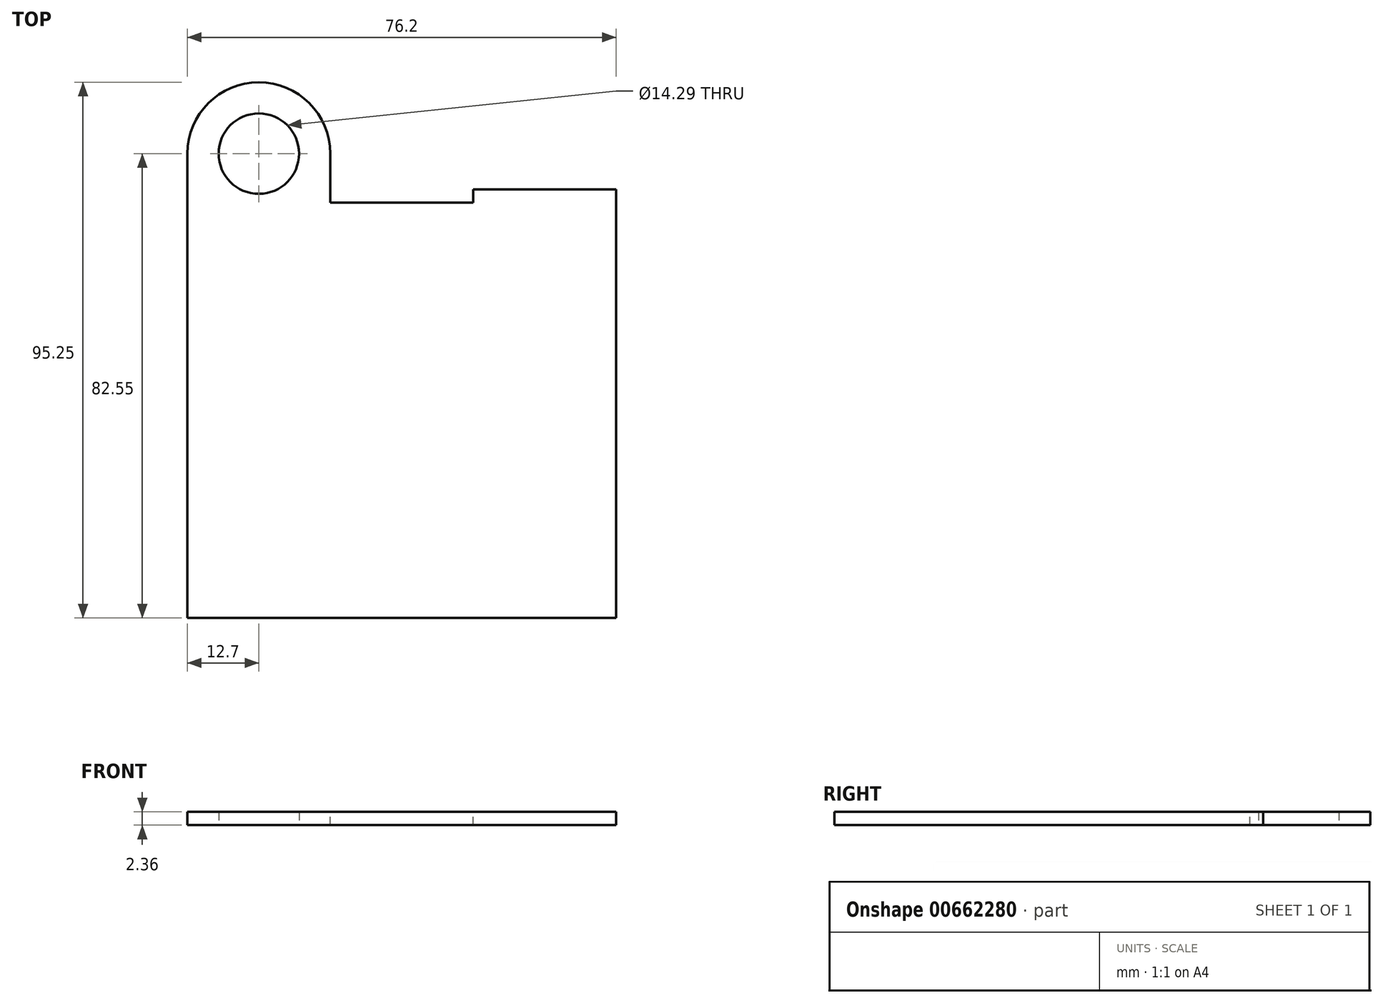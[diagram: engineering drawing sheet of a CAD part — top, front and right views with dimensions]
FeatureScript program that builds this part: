
annotation { "Feature Type Name" : "Feature", "Feature Type Description" : "" }
export const myFeature = defineFeature(function(context is Context, id is Id, definition is map)
    precondition{}
    {
        {
            var Q0;
            Q0=qCreatedBy(makeId("Top.planeOp"),FACE);
            var sketch = newSketch(context, id + "F0", { "sketchPlane" : qUnion([Q0])});
            skLineSegment(sketch, "E0.bottom", {"start": v(38.1, -38.1) * mm, "end": v(-38.1, -38.1) * mm});
            skLineSegment(sketch, "E0.top", {"start": v(38.1, 38.1) * mm, "end": v(-38.1, 38.1) * mm});
            skLineSegment(sketch, "E0.left", {"start": v(38.1, -38.1) * mm, "end": v(38.1, 38.1) * mm});
            skLineSegment(sketch, "E0.right", {"start": v(-38.1, -38.1) * mm, "end": v(-38.1, 38.1) * mm});
            skPoint(sketch, "E0.middle", {"position": v(0, 0) * mm});
            skSolve(sketch);
        }
        {
            var Q0;
            Q0=qSketchRegion(id+"F0",true);
            extrude(context, id + "F1", {"entities" : qUnion([Q0]), "depth" : 2.36 * mm, "offsetDistance" : 25.4 * mm});
        }
        {
            var Q0;
            Q0=makeQuery(id+"F1.opExtrude","CAP_FACE",FACE,{"disambiguationData":[OSD([sQuery(id+"F0.wireOp",EDGE,"E0.bottom"),sQuery(id+"F0.wireOp",EDGE,"E0.top"),sQuery(id+"F0.wireOp",EDGE,"E0.left"),sQuery(id+"F0.wireOp",EDGE,"E0.right")])],"isStart":false});
            var sketch = newSketch(context, id + "F2", { "sketchPlane" : qUnion([Q0])});
            skLineSegment(sketch, "E1.bottom", {"start": v(-12.7, 38.1) * mm, "end": v(12.7, 38.1) * mm});
            skLineSegment(sketch, "E1.top", {"start": v(-12.7, 35.74) * mm, "end": v(12.7, 35.74) * mm});
            skLineSegment(sketch, "E1.left", {"start": v(-12.7, 38.1) * mm, "end": v(-12.7, 35.74) * mm});
            skLineSegment(sketch, "E1.right", {"start": v(12.7, 38.1) * mm, "end": v(12.7, 35.74) * mm});
            skSolve(sketch);
        }
        {
            var Q0;
            Q0=qCreatedBy(makeId("Right.planeOp"),FACE);
            var sketch = newSketch(context, id + "F3", { "sketchPlane" : qUnion([Q0])});
            skLineSegment(sketch, "E2", {"start": v(0, 0) * mm, "end": v(0, 36.5) * mm});
            skSolve(sketch);
        }
        {
            var Q0;
            Q0=makeQuery(id+"F2.imprint","IMPRINT",FACE,{"disambiguationData":[TD([[makeQuery(id+"F2.imprint","IMPRINT",EDGE,{"derivedFrom":sQuery(id+"F2.wireOp",EDGE,"E1.bottom")}),1.0]])]});
            extrude(context, id + "F4", {"entities" : qUnion([Q0]), "operationType" : NewBodyOperationType.REMOVE, "oppositeDirection" : true, "depth" : 25.4 * mm, "offsetDistance" : 25.4 * mm});
        }
        {
            var Q0;
            Q0=makeQuery(id+"F1.opExtrude","CAP_FACE",FACE,{"disambiguationData":[OSD([sQuery(id+"F0.wireOp",EDGE,"E0.bottom"),sQuery(id+"F0.wireOp",EDGE,"E0.top"),sQuery(id+"F0.wireOp",EDGE,"E0.left"),sQuery(id+"F0.wireOp",EDGE,"E0.right")])],"isStart":false});
            var sketch = newSketch(context, id + "F5", { "sketchPlane" : qUnion([Q0])});
            skLineSegment(sketch, "E3.bottom", {"start": v(-38.1, 38.1) * mm, "end": v(-12.7, 38.1) * mm});
            skLineSegment(sketch, "E3.left", {"start": v(-38.1, 38.1) * mm, "end": v(-38.1, 44.45) * mm});
            skLineSegment(sketch, "E3.right", {"start": v(-12.7, 38.1) * mm, "end": v(-12.7, 44.45) * mm});
            skArc(sketch, "E4", {"start": v(-12.7, 44.45) * mm, "mid": v(-25.4, 57.15) * mm, "end": v(-38.1, 44.45) * mm});
            skSolve(sketch);
        }
        {
            var Q0;
            Q0 = qSketchRegion(id + "F5", true);
            var Q1;
            Q1=makeQuery(id+"F1.opExtrude","CAP_FACE",FACE,{"disambiguationData":[OSD([sQuery(id+"F0.wireOp",EDGE,"E0.bottom"),sQuery(id+"F0.wireOp",EDGE,"E0.top"),sQuery(id+"F0.wireOp",EDGE,"E0.left"),sQuery(id+"F0.wireOp",EDGE,"E0.right")])],"isStart":true});
            extrude(context, id + "F6", {"entities" : qUnion([Q0]), "operationType" : NewBodyOperationType.ADD, "endBound" : BoundingType.UP_TO_SURFACE, "oppositeDirection" : true, "depth" : 25.4 * mm, "endBoundEntityFace" : qUnion([Q1]), "offsetDistance" : 25.4 * mm});
        }
        {
            var Q0;
            Q0=qCreatedBy(makeId("Top.planeOp"),FACE);
            var sketch = newSketch(context, id + "F7", { "sketchPlane" : qUnion([Q0])});
            skCircle(sketch, "E5", {"center": v(-25.4, 44.45) * mm, "radius": 7.14 * mm});
            skSolve(sketch);
        }
        {
            var Q0;
            Q0=makeQuery(id+"F7.imprint","IMPRINT",FACE,{"disambiguationData":[TD([[makeQuery(id+"F7.imprint","IMPRINT",EDGE,{"derivedFrom":sQuery(id+"F7.wireOp",EDGE,"E5")}),1.0]])]});
            extrude(context, id + "F8", {"entities" : qUnion([Q0]), "operationType" : NewBodyOperationType.REMOVE, "endBound" : BoundingType.THROUGH_ALL, "depth" : 25.4 * mm, "offsetDistance" : 25.4 * mm});
        }
    });
